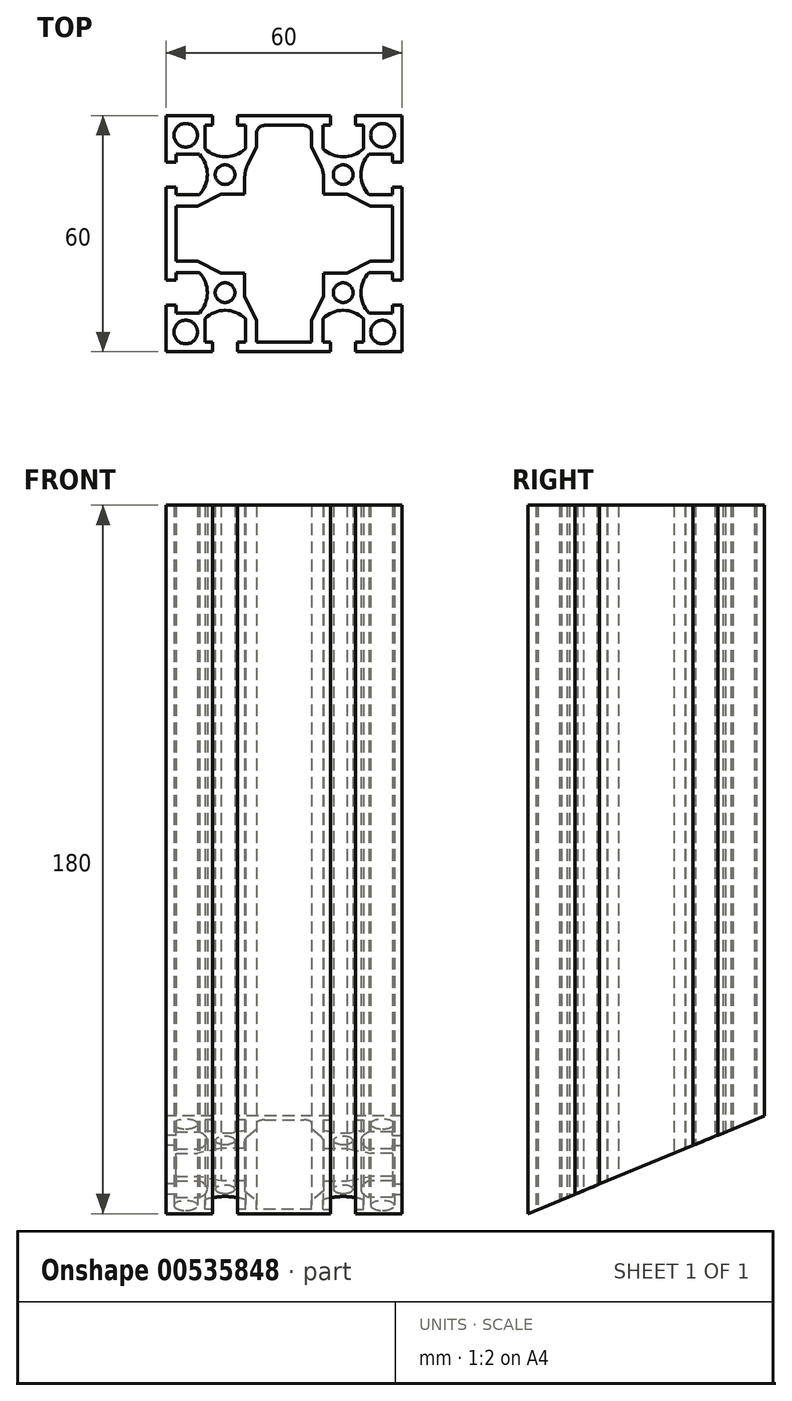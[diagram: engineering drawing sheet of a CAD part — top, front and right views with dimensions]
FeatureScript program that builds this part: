
annotation { "Feature Type Name" : "Feature", "Feature Type Description" : "" }
export const myFeature = defineFeature(function(context is Context, id is Id, definition is map)
    precondition{}
    {
        {
            var Q0;
            Q0=qCreatedBy(makeId("Top.planeOp"),FACE);
            var sketch = newSketch(context, id + "F0", { "sketchPlane" : qUnion([Q0])});
            skLineSegment(sketch, "E0.bottom", {"start": v(30, -30) * mm, "end": v(-30, -30) * mm});
            skLineSegment(sketch, "E0.top", {"start": v(30, 30) * mm, "end": v(-30, 30) * mm});
            skLineSegment(sketch, "E0.left", {"start": v(30, -30) * mm, "end": v(30, 30) * mm});
            skLineSegment(sketch, "E0.right", {"start": v(-30, -30) * mm, "end": v(-30, 30) * mm});
            skPoint(sketch, "E0.middle", {"position": v(0, 0) * mm});
            skLineSegment(sketch, "E1.top", {"start": v(-11.85, 30) * mm, "end": v(-18.15, 30) * mm});
            skLineSegment(sketch, "E1.left", {"start": v(-11.85, 27.5) * mm, "end": v(-11.85, 30) * mm});
            skLineSegment(sketch, "E1.right", {"start": v(-18.15, 27.5) * mm, "end": v(-18.15, 30) * mm});
            skPoint(sketch, "E1.middle", {"position": v(-15, 28.75) * mm});
            skLineSegment(sketch, "E2.bottom", {"start": v(-9.85, 27.5) * mm, "end": v(-11.85, 27.5) * mm});
            skLineSegment(sketch, "E2.left", {"start": v(-9.85, 27.5) * mm, "end": v(-9.85, 21.55) * mm});
            skLineSegment(sketch, "E2.right", {"start": v(-20.15, 27.5) * mm, "end": v(-20.15, 21.55) * mm});
            skPoint(sketch, "E2.middle", {"position": v(-15, 24.52) * mm});
            skArc(sketch, "E3", {"start": v(-20.15, 21.55) * mm, "mid": v(-15, 19.5) * mm, "end": v(-9.85, 21.55) * mm});
            skPoint(sketch, "E4.MirrorP", {"position": v(15, 24.52) * mm});
            skPoint(sketch, "E5.MirrorP", {"position": v(15, 28.75) * mm});
            skLineSegment(sketch, "E6.MirrorCS", {"start": v(11.85, 27.5) * mm, "end": v(11.85, 30) * mm});
            skLineSegment(sketch, "E7.MirrorCS", {"start": v(18.15, 27.5) * mm, "end": v(18.15, 30) * mm});
            skLineSegment(sketch, "E8.MirrorCS", {"start": v(9.85, 27.5) * mm, "end": v(11.85, 27.5) * mm});
            skLineSegment(sketch, "E9.MirrorCS", {"start": v(9.85, 27.5) * mm, "end": v(9.85, 21.55) * mm});
            skArc(sketch, "E10.MirrorCS", {"start": v(20.15, 21.55) * mm, "mid": v(15, 19.5) * mm, "end": v(9.85, 21.55) * mm});
            skLineSegment(sketch, "E11.MirrorCS", {"start": v(20.15, 27.5) * mm, "end": v(20.15, 21.55) * mm});
            skLineSegment(sketch, "E12.MirrorCS", {"start": v(11.85, 30) * mm, "end": v(18.15, 30) * mm});
            skLineSegment(sketch, "E13.1.0", {"start": v(27.5, 20.15) * mm, "end": v(21.55, 20.15) * mm});
            skLineSegment(sketch, "E13.1.1", {"start": v(27.5, 9.85) * mm, "end": v(21.55, 9.85) * mm});
            skArc(sketch, "E13.1.2", {"start": v(21.55, 20.15) * mm, "mid": v(19.5, 15) * mm, "end": v(21.55, 9.85) * mm});
            skLineSegment(sketch, "E13.1.3", {"start": v(27.5, -9.85) * mm, "end": v(21.55, -9.85) * mm});
            skLineSegment(sketch, "E13.1.4", {"start": v(27.5, -20.15) * mm, "end": v(21.55, -20.15) * mm});
            skPoint(sketch, "E13.1.5", {"position": v(28.75, 15) * mm});
            skPoint(sketch, "E13.1.6", {"position": v(28.75, -15) * mm});
            skArc(sketch, "E13.1.7", {"start": v(21.55, -20.15) * mm, "mid": v(19.5, -15) * mm, "end": v(21.55, -9.85) * mm});
            skPoint(sketch, "E13.1.8", {"position": v(24.52, -15) * mm});
            skPoint(sketch, "E13.1.9", {"position": v(24.52, 15) * mm});
            skLineSegment(sketch, "E13.1.10", {"start": v(27.5, 9.85) * mm, "end": v(27.5, 20.15) * mm});
            skLineSegment(sketch, "E13.1.11", {"start": v(27.5, -11.85) * mm, "end": v(27.5, -18.15) * mm});
            skLineSegment(sketch, "E13.1.12", {"start": v(30, 11.85) * mm, "end": v(30, 18.15) * mm});
            skLineSegment(sketch, "E13.1.13", {"start": v(30, -11.85) * mm, "end": v(30, -18.15) * mm});
            skLineSegment(sketch, "E13.1.14", {"start": v(27.5, 18.15) * mm, "end": v(30, 18.15) * mm});
            skLineSegment(sketch, "E13.1.15", {"start": v(27.5, 11.85) * mm, "end": v(30, 11.85) * mm});
            skLineSegment(sketch, "E13.1.16", {"start": v(27.5, 11.85) * mm, "end": v(27.5, 18.15) * mm});
            skLineSegment(sketch, "E13.1.17", {"start": v(27.5, -9.85) * mm, "end": v(27.5, -20.15) * mm});
            skLineSegment(sketch, "E13.1.18", {"start": v(27.5, -18.15) * mm, "end": v(30, -18.15) * mm});
            skLineSegment(sketch, "E13.1.19", {"start": v(27.5, -11.85) * mm, "end": v(30, -11.85) * mm});
            skLineSegment(sketch, "E13.2.0", {"start": v(20.15, -27.5) * mm, "end": v(20.15, -21.55) * mm});
            skLineSegment(sketch, "E13.2.1", {"start": v(9.85, -27.5) * mm, "end": v(9.85, -21.55) * mm});
            skArc(sketch, "E13.2.2", {"start": v(20.15, -21.55) * mm, "mid": v(15, -19.5) * mm, "end": v(9.85, -21.55) * mm});
            skLineSegment(sketch, "E13.2.3", {"start": v(-9.85, -27.5) * mm, "end": v(-9.85, -21.55) * mm});
            skLineSegment(sketch, "E13.2.4", {"start": v(-20.15, -27.5) * mm, "end": v(-20.15, -21.55) * mm});
            skPoint(sketch, "E13.2.5", {"position": v(15, -28.75) * mm});
            skPoint(sketch, "E13.2.6", {"position": v(-15, -28.75) * mm});
            skArc(sketch, "E13.2.7", {"start": v(-20.15, -21.55) * mm, "mid": v(-15, -19.5) * mm, "end": v(-9.85, -21.55) * mm});
            skPoint(sketch, "E13.2.8", {"position": v(-15, -24.52) * mm});
            skPoint(sketch, "E13.2.9", {"position": v(15, -24.52) * mm});
            skLineSegment(sketch, "E13.2.10", {"start": v(9.85, -27.5) * mm, "end": v(20.15, -27.5) * mm});
            skLineSegment(sketch, "E13.2.11", {"start": v(-11.85, -27.5) * mm, "end": v(-18.15, -27.5) * mm});
            skLineSegment(sketch, "E13.2.12", {"start": v(11.85, -30) * mm, "end": v(18.15, -30) * mm});
            skLineSegment(sketch, "E13.2.13", {"start": v(-11.85, -30) * mm, "end": v(-18.15, -30) * mm});
            skLineSegment(sketch, "E13.2.14", {"start": v(18.15, -27.5) * mm, "end": v(18.15, -30) * mm});
            skLineSegment(sketch, "E13.2.15", {"start": v(11.85, -27.5) * mm, "end": v(11.85, -30) * mm});
            skLineSegment(sketch, "E13.2.16", {"start": v(11.85, -27.5) * mm, "end": v(18.15, -27.5) * mm});
            skLineSegment(sketch, "E13.2.17", {"start": v(-9.85, -27.5) * mm, "end": v(-20.15, -27.5) * mm});
            skLineSegment(sketch, "E13.2.18", {"start": v(-18.15, -27.5) * mm, "end": v(-18.15, -30) * mm});
            skLineSegment(sketch, "E13.2.19", {"start": v(-11.85, -27.5) * mm, "end": v(-11.85, -30) * mm});
            skLineSegment(sketch, "E13.3.0", {"start": v(-27.5, -20.15) * mm, "end": v(-21.55, -20.15) * mm});
            skLineSegment(sketch, "E13.3.1", {"start": v(-27.5, -9.85) * mm, "end": v(-21.55, -9.85) * mm});
            skArc(sketch, "E13.3.2", {"start": v(-21.55, -20.15) * mm, "mid": v(-19.5, -15) * mm, "end": v(-21.55, -9.85) * mm});
            skLineSegment(sketch, "E13.3.3", {"start": v(-27.5, 9.85) * mm, "end": v(-21.55, 9.85) * mm});
            skLineSegment(sketch, "E13.3.4", {"start": v(-27.5, 20.15) * mm, "end": v(-21.55, 20.15) * mm});
            skPoint(sketch, "E13.3.5", {"position": v(-28.75, -15) * mm});
            skPoint(sketch, "E13.3.6", {"position": v(-28.75, 15) * mm});
            skArc(sketch, "E13.3.7", {"start": v(-21.55, 20.15) * mm, "mid": v(-19.5, 15) * mm, "end": v(-21.55, 9.85) * mm});
            skPoint(sketch, "E13.3.8", {"position": v(-24.52, 15) * mm});
            skPoint(sketch, "E13.3.9", {"position": v(-24.52, -15) * mm});
            skLineSegment(sketch, "E13.3.10", {"start": v(-27.5, -9.85) * mm, "end": v(-27.5, -20.15) * mm});
            skLineSegment(sketch, "E13.3.11", {"start": v(-27.5, 11.85) * mm, "end": v(-27.5, 18.15) * mm});
            skLineSegment(sketch, "E13.3.12", {"start": v(-30, -11.85) * mm, "end": v(-30, -18.15) * mm});
            skLineSegment(sketch, "E13.3.13", {"start": v(-30, 11.85) * mm, "end": v(-30, 18.15) * mm});
            skLineSegment(sketch, "E13.3.14", {"start": v(-27.5, -18.15) * mm, "end": v(-30, -18.15) * mm});
            skLineSegment(sketch, "E13.3.15", {"start": v(-27.5, -11.85) * mm, "end": v(-30, -11.85) * mm});
            skLineSegment(sketch, "E13.3.16", {"start": v(-27.5, -11.85) * mm, "end": v(-27.5, -18.15) * mm});
            skLineSegment(sketch, "E13.3.17", {"start": v(-27.5, 9.85) * mm, "end": v(-27.5, 20.15) * mm});
            skLineSegment(sketch, "E13.3.18", {"start": v(-27.5, 18.15) * mm, "end": v(-30, 18.15) * mm});
            skLineSegment(sketch, "E13.3.19", {"start": v(-27.5, 11.85) * mm, "end": v(-30, 11.85) * mm});
            skLineSegment(sketch, "E13.anchor1", {"start": v(0, 0) * mm, "end": v(-20.15, 21.55) * mm, "construction": true});
            skLineSegment(sketch, "E13.anchor2", {"start": v(0, 0) * mm, "end": v(-21.55, -20.15) * mm, "construction": true});
            skLineSegment(sketch, "E14.trimOffspring", {"start": v(-18.15, 27.5) * mm, "end": v(-20.15, 27.5) * mm});
            skLineSegment(sketch, "E15.trimOffspring", {"start": v(18.15, 27.5) * mm, "end": v(20.15, 27.5) * mm});
            skCircle(sketch, "E16", {"center": v(-15, 15) * mm, "radius": 2.5 * mm});
            skCircle(sketch, "E17", {"center": v(-25, 25) * mm, "radius": 3 * mm});
            skCircle(sketch, "E18.MirrorC", {"center": v(25, 25) * mm, "radius": 3 * mm});
            skCircle(sketch, "E19.MirrorC", {"center": v(25, -25) * mm, "radius": 3 * mm});
            skCircle(sketch, "E20.MirrorC", {"center": v(-25, -25) * mm, "radius": 3 * mm});
            skCircle(sketch, "E21.MirrorC", {"center": v(15, 15) * mm, "radius": 2.5 * mm});
            skCircle(sketch, "E22.MirrorC", {"center": v(15, -15) * mm, "radius": 2.5 * mm});
            skCircle(sketch, "E23.MirrorC", {"center": v(-15, -15) * mm, "radius": 2.5 * mm});
            skLineSegment(sketch, "E24", {"start": v(-7, 27.5) * mm, "end": v(0, 27.5) * mm});
            skLineSegment(sketch, "E25", {"start": v(-7, 27.5) * mm, "end": v(-7, 22) * mm});
            skLineSegment(sketch, "E26", {"start": v(-10, 10) * mm, "end": v(-10, 16) * mm});
            skLineSegment(sketch, "E27", {"start": v(-10, 16) * mm, "end": v(-7, 22) * mm});
            skLineSegment(sketch, "E28.MirrorCS", {"start": v(10, 10) * mm, "end": v(10, 16) * mm});
            skLineSegment(sketch, "E29.MirrorCS", {"start": v(10, 16) * mm, "end": v(7, 22) * mm});
            skLineSegment(sketch, "E30.MirrorCS", {"start": v(7, 27.5) * mm, "end": v(0, 27.5) * mm});
            skLineSegment(sketch, "E31.MirrorCS", {"start": v(7, 27.5) * mm, "end": v(7, 22) * mm});
            skLineSegment(sketch, "E32.1.0", {"start": v(-10, -10) * mm, "end": v(-16, -10) * mm});
            skLineSegment(sketch, "E32.1.1", {"start": v(-16, -10) * mm, "end": v(-22, -7) * mm});
            skLineSegment(sketch, "E32.1.2", {"start": v(-27.5, -7) * mm, "end": v(-22, -7) * mm});
            skLineSegment(sketch, "E32.1.3", {"start": v(-27.5, -7) * mm, "end": v(-27.5, 0) * mm});
            skLineSegment(sketch, "E32.1.4", {"start": v(-27.5, 7) * mm, "end": v(-27.5, 0) * mm});
            skLineSegment(sketch, "E32.1.5", {"start": v(-27.5, 7) * mm, "end": v(-22, 7) * mm});
            skLineSegment(sketch, "E32.1.6", {"start": v(-16, 10) * mm, "end": v(-22, 7) * mm});
            skLineSegment(sketch, "E32.1.7", {"start": v(-10, 10) * mm, "end": v(-16, 10) * mm});
            skLineSegment(sketch, "E32.2.0", {"start": v(10, -10) * mm, "end": v(10, -16) * mm});
            skLineSegment(sketch, "E32.2.1", {"start": v(10, -16) * mm, "end": v(7, -22) * mm});
            skLineSegment(sketch, "E32.2.2", {"start": v(7, -27.5) * mm, "end": v(7, -22) * mm});
            skLineSegment(sketch, "E32.2.3", {"start": v(7, -27.5) * mm, "end": v(0, -27.5) * mm});
            skLineSegment(sketch, "E32.2.4", {"start": v(-7, -27.5) * mm, "end": v(0, -27.5) * mm});
            skLineSegment(sketch, "E32.2.5", {"start": v(-7, -27.5) * mm, "end": v(-7, -22) * mm});
            skLineSegment(sketch, "E32.2.6", {"start": v(-10, -16) * mm, "end": v(-7, -22) * mm});
            skLineSegment(sketch, "E32.2.7", {"start": v(-10, -10) * mm, "end": v(-10, -16) * mm});
            skLineSegment(sketch, "E32.3.0", {"start": v(10, 10) * mm, "end": v(16, 10) * mm});
            skLineSegment(sketch, "E32.3.1", {"start": v(16, 10) * mm, "end": v(22, 7) * mm});
            skLineSegment(sketch, "E32.3.2", {"start": v(27.5, 7) * mm, "end": v(22, 7) * mm});
            skLineSegment(sketch, "E32.3.3", {"start": v(27.5, 7) * mm, "end": v(27.5, 0) * mm});
            skLineSegment(sketch, "E32.3.4", {"start": v(27.5, -7) * mm, "end": v(27.5, 0) * mm});
            skLineSegment(sketch, "E32.3.5", {"start": v(27.5, -7) * mm, "end": v(22, -7) * mm});
            skLineSegment(sketch, "E32.3.6", {"start": v(16, -10) * mm, "end": v(22, -7) * mm});
            skLineSegment(sketch, "E32.3.7", {"start": v(10, -10) * mm, "end": v(16, -10) * mm});
            skSolve(sketch);
        }
        {
            var Q0;
            {var subQ30=sQuery(id+"F0.wireOp",EDGE,"E1.left");Q0=makeQuery(id+"F0.imprint","IMPRINT",FACE,{"disambiguationData":[TD([[makeQuery(id+"F0.imprint","IMPRINT",EDGE,{"derivedFrom":subQ30}),-1.0]])]});}
            extrude(context, id + "F1", {"entities" : qUnion([Q0]), "depth" : 180 * mm, "offsetDistance" : 25 * mm});
        }
        {
            var Q0;
            Q0=makeQuery(id+"F1.opExtrude","SWEPT_EDGE",EDGE,{"disambiguationData":[OSD([sQuery(id+"F0.wireOp",EDGE,"E24"),sQuery(id+"F0.wireOp",EDGE,"E25")])]});
            var Q1;
            Q1=makeQuery(id+"F1.opExtrude","SWEPT_EDGE",EDGE,{"disambiguationData":[OSD([sQuery(id+"F0.wireOp",EDGE,"E30.MirrorCS"),sQuery(id+"F0.wireOp",EDGE,"E31.MirrorCS")])]});
            var Q2;
            Q2=makeQuery(id+"F1.opExtrude","SWEPT_EDGE",EDGE,{"disambiguationData":[OSD([sQuery(id+"F0.wireOp",EDGE,"840db5bc-c403-45cd-90c7-254e62d9e8c5.3.2"),sQuery(id+"F0.wireOp",EDGE,"840db5bc-c403-45cd-90c7-254e62d9e8c5.3.3")])]});
            var Q3;
            Q3=makeQuery(id+"F1.opExtrude","SWEPT_EDGE",EDGE,{"disambiguationData":[OSD([sQuery(id+"F0.wireOp",EDGE,"840db5bc-c403-45cd-90c7-254e62d9e8c5.3.4"),sQuery(id+"F0.wireOp",EDGE,"840db5bc-c403-45cd-90c7-254e62d9e8c5.3.5")])]});
            var Q4;
            Q4=makeQuery(id+"F1.opExtrude","SWEPT_EDGE",EDGE,{"disambiguationData":[OSD([sQuery(id+"F0.wireOp",EDGE,"840db5bc-c403-45cd-90c7-254e62d9e8c5.1.4"),sQuery(id+"F0.wireOp",EDGE,"840db5bc-c403-45cd-90c7-254e62d9e8c5.1.5")])]});
            var Q5;
            Q5=makeQuery(id+"F1.opExtrude","SWEPT_EDGE",EDGE,{"disambiguationData":[OSD([sQuery(id+"F0.wireOp",EDGE,"840db5bc-c403-45cd-90c7-254e62d9e8c5.1.2"),sQuery(id+"F0.wireOp",EDGE,"840db5bc-c403-45cd-90c7-254e62d9e8c5.1.3")])]});
            var Q6;
            Q6=makeQuery(id+"F1.opExtrude","SWEPT_EDGE",EDGE,{"disambiguationData":[OSD([sQuery(id+"F0.wireOp",EDGE,"840db5bc-c403-45cd-90c7-254e62d9e8c5.2.2"),sQuery(id+"F0.wireOp",EDGE,"840db5bc-c403-45cd-90c7-254e62d9e8c5.2.3")])]});
            var Q7;
            Q7=makeQuery(id+"F1.opExtrude","SWEPT_EDGE",EDGE,{"disambiguationData":[OSD([sQuery(id+"F0.wireOp",EDGE,"840db5bc-c403-45cd-90c7-254e62d9e8c5.2.4"),sQuery(id+"F0.wireOp",EDGE,"840db5bc-c403-45cd-90c7-254e62d9e8c5.2.5")])]});
            fillet(context, id + "F2", {"entities" : qUnion([Q0, Q1, Q2, Q3, Q4, Q5, Q6, Q7]), "radius" : 2 * mm, "tangentPropagation" : true, "allowEdgeOverflow" : false});
        }
        {
            var Q0;
            Q0=makeQuery(id+"F1.opExtrude","SWEPT_EDGE",EDGE,{"disambiguationData":[OSD([sQuery(id+"F0.wireOp",EDGE,"E26"),sQuery(id+"F0.wireOp",EDGE,"E27")])]});
            var Q1;
            Q1=makeQuery(id+"F1.opExtrude","SWEPT_EDGE",EDGE,{"disambiguationData":[OSD([sQuery(id+"F0.wireOp",EDGE,"E28.MirrorCS"),sQuery(id+"F0.wireOp",EDGE,"E29.MirrorCS")])]});
            var Q2;
            Q2=makeQuery(id+"F1.opExtrude","SWEPT_EDGE",EDGE,{"disambiguationData":[OSD([sQuery(id+"F0.wireOp",EDGE,"840db5bc-c403-45cd-90c7-254e62d9e8c5.3.0"),sQuery(id+"F0.wireOp",EDGE,"840db5bc-c403-45cd-90c7-254e62d9e8c5.3.1")])]});
            var Q3;
            Q3=makeQuery(id+"F1.opExtrude","SWEPT_EDGE",EDGE,{"disambiguationData":[OSD([sQuery(id+"F0.wireOp",EDGE,"840db5bc-c403-45cd-90c7-254e62d9e8c5.1.6"),sQuery(id+"F0.wireOp",EDGE,"840db5bc-c403-45cd-90c7-254e62d9e8c5.1.7")])]});
            var Q4;
            Q4=makeQuery(id+"F1.opExtrude","SWEPT_EDGE",EDGE,{"disambiguationData":[OSD([sQuery(id+"F0.wireOp",EDGE,"840db5bc-c403-45cd-90c7-254e62d9e8c5.1.0"),sQuery(id+"F0.wireOp",EDGE,"840db5bc-c403-45cd-90c7-254e62d9e8c5.1.1")])]});
            var Q5;
            Q5=makeQuery(id+"F1.opExtrude","SWEPT_EDGE",EDGE,{"disambiguationData":[OSD([sQuery(id+"F0.wireOp",EDGE,"840db5bc-c403-45cd-90c7-254e62d9e8c5.3.6"),sQuery(id+"F0.wireOp",EDGE,"840db5bc-c403-45cd-90c7-254e62d9e8c5.3.7")])]});
            var Q6;
            Q6=makeQuery(id+"F1.opExtrude","SWEPT_EDGE",EDGE,{"disambiguationData":[OSD([sQuery(id+"F0.wireOp",EDGE,"840db5bc-c403-45cd-90c7-254e62d9e8c5.2.0"),sQuery(id+"F0.wireOp",EDGE,"840db5bc-c403-45cd-90c7-254e62d9e8c5.2.1")])]});
            var Q7;
            Q7=makeQuery(id+"F1.opExtrude","SWEPT_EDGE",EDGE,{"disambiguationData":[OSD([sQuery(id+"F0.wireOp",EDGE,"840db5bc-c403-45cd-90c7-254e62d9e8c5.2.6"),sQuery(id+"F0.wireOp",EDGE,"840db5bc-c403-45cd-90c7-254e62d9e8c5.2.7")])]});
            fillet(context, id + "F3", {"entities" : qUnion([Q0, Q1, Q2, Q3, Q4, Q5, Q6, Q7]), "radius" : 7 * mm, "tangentPropagation" : true, "allowEdgeOverflow" : false});
        }
        {
            var Q0;
            {var subQ0=sQuery(id+"F0.wireOp",EDGE,"E0.bottom");Q0=makeQuery(id+"F1.opExtrude","SWEPT_FACE",FACE,{"disambiguationData":[OSD([subQ0]),TDD([makeQuery(id+"F0.imprint","IMPRINT",EDGE,{"disambiguationData":[TD([[makeQuery(id+"F0.imprint","INTERSECT",VERTEX,{"derivedFrom":[subQ0,sQuery(id+"F0.wireOp",EDGE,"E13.2.12"),sQuery(id+"F0.wireOp",EDGE,"E13.2.15")]}),-1.0]])],"derivedFrom":subQ0})])]});}
            var sketch = newSketch(context, id + "F4", { "sketchPlane" : qUnion([Q0])});
            skLineSegment(sketch, "E33.0", {"start": v(-18.15, 180) * mm, "end": v(-30, 180) * mm});
            skLineSegment(sketch, "E33.1", {"start": v(30, 180) * mm, "end": v(30, 0) * mm});
            skLineSegment(sketch, "E34", {"start": v(-30, 180) * mm, "end": v(30, 180) * mm});
            skLineSegment(sketch, "E35", {"start": v(30, 120) * mm, "end": v(-30, 180) * mm});
            skLineSegment(sketch, "E36.0", {"start": v(-18.15, 0) * mm, "end": v(-30, 0) * mm});
            skLineSegment(sketch, "E37", {"start": v(-30, 0) * mm, "end": v(30, 0) * mm});
            skLineSegment(sketch, "E38", {"start": v(30, 60) * mm, "end": v(-30, 0) * mm});
            skSolve(sketch);
        }
        {
            var Q0;
            Q0=qCreatedBy(makeId("Right.planeOp"),FACE);
            var sketch = newSketch(context, id + "F5", { "sketchPlane" : qUnion([Q0])});
            skLineSegment(sketch, "E39.bottom", {"start": v(145.98, 72.9) * mm, "end": v(-30, 0) * mm});
            skLineSegment(sketch, "E39.top", {"start": v(189.02, -31) * mm, "end": v(13.04, -103.9) * mm});
            skLineSegment(sketch, "E39.left", {"start": v(145.98, 72.9) * mm, "end": v(189.02, -31) * mm});
            skLineSegment(sketch, "E39.right", {"start": v(-30, 0) * mm, "end": v(13.04, -103.9) * mm});
            skSolve(sketch);
        }
        {
            var Q0;
            Q0 = qSketchRegion(id + "F5", true);
            extrude(context, id + "F6", {"entities" : qUnion([Q0]), "operationType" : NewBodyOperationType.REMOVE, "oppositeDirection" : true, "depth" : 30 * mm, "offsetDistance" : 25 * mm, "hasSecondDirection" : true, "secondDirectionOppositeDirection" : false, "secondDirectionDepth" : 30 * mm});
        }
    });
